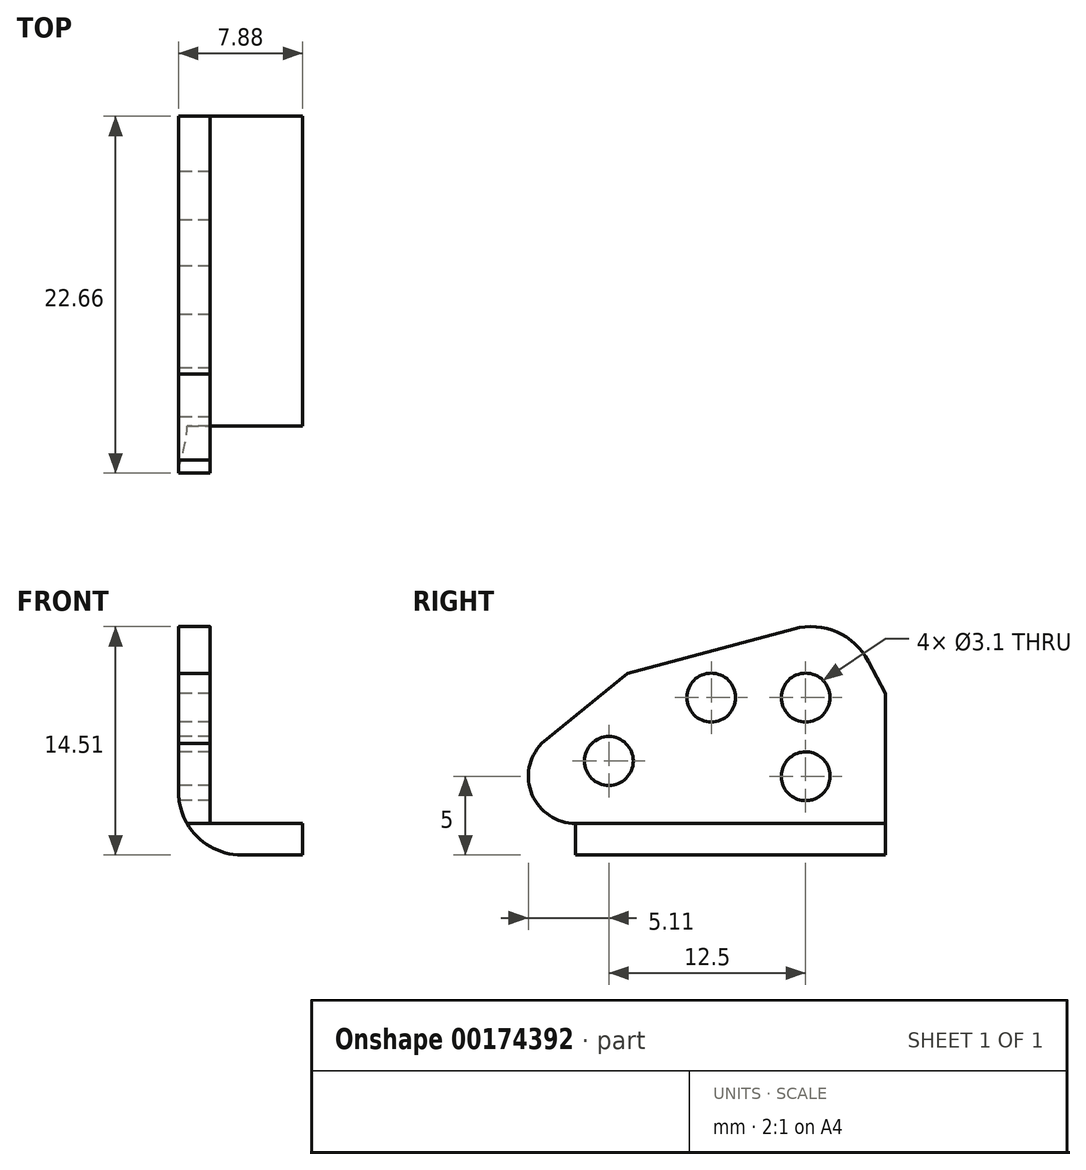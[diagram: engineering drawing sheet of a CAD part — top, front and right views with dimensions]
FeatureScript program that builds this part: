
annotation { "Feature Type Name" : "Feature", "Feature Type Description" : "" }
export const myFeature = defineFeature(function(context is Context, id is Id, definition is map)
    precondition{}
    {
        {
            var Q0;
            Q0=qCreatedBy(makeId("Right.planeOp"),FACE);
            var sketch = newSketch(context, id + "F0", { "sketchPlane" : qUnion([Q0])});
            skCircle(sketch, "E0", {"center": v(0, 0) * mm, "radius": 1.55 * mm});
            skCircle(sketch, "E1", {"center": v(0, 5) * mm, "radius": 1.55 * mm});
            skCircle(sketch, "E2", {"center": v(-6, 5) * mm, "radius": 1.55 * mm});
            skLineSegment(sketch, "E3", {"start": v(-13.22, -3) * mm, "end": v(-14.61, -3) * mm});
            skArc(sketch, "E4", {"start": v(-14.61, -3) * mm, "mid": v(-17.37, -1.17) * mm, "end": v(-16.77, 2.08) * mm});
            skLineSegment(sketch, "E5", {"start": v(-16.77, 2.08) * mm, "end": v(-11.32, 6.54) * mm});
            skLineSegment(sketch, "E6", {"start": v(-11.32, 6.54) * mm, "end": v(-0.75, 9.37) * mm});
            skArc(sketch, "E7", {"start": v(-0.75, 9.37) * mm, "mid": v(1.98, 9.16) * mm, "end": v(3.99, 7.3) * mm});
            skLineSegment(sketch, "E8", {"start": v(3.99, 7.3) * mm, "end": v(5.05, 5.27) * mm});
            skLineSegment(sketch, "E9", {"start": v(5.05, 5.27) * mm, "end": v(5.05, -3) * mm});
            skLineSegment(sketch, "E10", {"start": v(5.05, -3) * mm, "end": v(-13.22, -3) * mm});
            skCircle(sketch, "E11", {"center": v(-12.5, 0.97) * mm, "radius": 1.55 * mm});
            skSolve(sketch);
        }
        {
            var Q0;
            Q0=makeQuery(id+"F0.imprint","IMPRINT",FACE,{"disambiguationData":[TD([[makeQuery(id+"F0.imprint","IMPRINT",EDGE,{"derivedFrom":sQuery(id+"F0.wireOp",EDGE,"E0")}),-1.0]])]});
            extrude(context, id + "F1", {"entities" : qUnion([Q0]), "depth" : 2 * mm});
        }
        {
            var Q0;
            Q0=makeQuery(id+"F1.opExtrude","SWEPT_FACE",FACE,{"disambiguationData":[OSD([sQuery(id+"F0.wireOp",EDGE,"E3"),sQuery(id+"F0.wireOp",EDGE,"E10")])]});
            var sketch = newSketch(context, id + "F2", { "sketchPlane" : qUnion([Q0])});
            skLineSegment(sketch, "E12.bottom", {"start": v(0, 14.61) * mm, "end": v(7.88, 14.61) * mm});
            skLineSegment(sketch, "E12.top", {"start": v(0, -5.05) * mm, "end": v(7.88, -5.05) * mm});
            skLineSegment(sketch, "E12.left", {"start": v(0, 14.61) * mm, "end": v(0, -5.05) * mm});
            skLineSegment(sketch, "E12.right", {"start": v(7.88, 14.61) * mm, "end": v(7.88, -5.05) * mm});
            skSolve(sketch);
        }
        {
            var Q0;
            {var subQ2=sQuery(id+"F2.wireOp",EDGE,"E12.right");Q0=makeQuery(id+"F2.imprint","IMPRINT",FACE,{"disambiguationData":[TD([[makeQuery(id+"F2.imprint","IMPRINT",EDGE,{"derivedFrom":subQ2}),-1.0]])]});}
            var Q1;
            {var subQ0=sQuery(id+"F2.wireOp",EDGE,"E12.left");Q1=makeQuery(id+"F2.imprint","IMPRINT",FACE,{"disambiguationData":[TD([[makeQuery(id+"F2.imprint","IMPRINT",EDGE,{"derivedFrom":subQ0}),-1.0]])]});}
            extrude(context, id + "F3", {"entities" : qUnion([Q0, Q1]), "operationType" : NewBodyOperationType.ADD, "depth" : 2 * mm});
        }
        {
            var Q0;
            Q0=makeQuery(id+"F3.opExtrude","CAP_EDGE",EDGE,{"disambiguationData":[OSD([sQuery(id+"F2.wireOp",EDGE,"E12.left")])],"isStart":false});
            fillet(context, id + "F4", {"entities" : qUnion([Q0]), "radius" : 4 * mm, "tangentPropagation" : true, "allowEdgeOverflow" : false});
        }
    });
